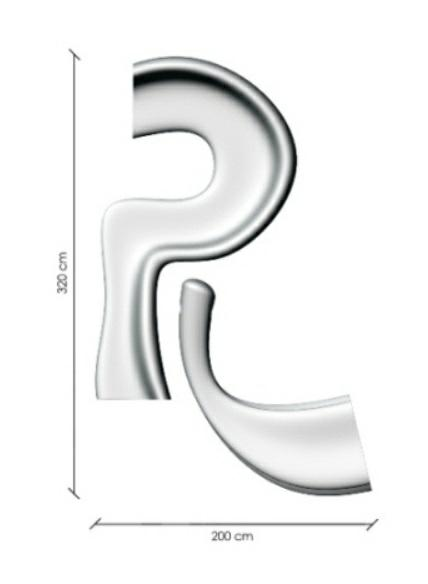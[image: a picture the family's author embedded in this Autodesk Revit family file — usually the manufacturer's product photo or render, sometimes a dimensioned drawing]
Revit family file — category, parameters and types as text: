
# Revit family: CITY ALPHABET litera „R”
name_source: partatom
category: Meble
revit_build: Autodesk Revit 2018 (Build: 20190510_1515(x64)
units: mm (PartAtom-declared; Revit-internal decimal feet)

## family parameters
Numer OmniClass = 23.40.10.11.14
Obiekt nadrzędny = Powierzchnia
Punkt obliczania pomieszczeń = Nie
Tnij formami wycięć po wczytaniu = Nie
Tytuł OmniClass = Exterior Seating
Współdzielony = Nie

## types (1)
- CITY ALPHABET litera „R”
    Domyślna rzędna = 1219 mm
    Długość = 2000 mm  [stored 6.56168 ft]
    IfcExportAs = IfcFurnishingElement
    Komentarze do typu = Ławka
    Materiał - informacja = Szeroki wybór kolorów wg palety RAL. Istnieje również możliwość specjalnego wykonania
kolorystycznego na indywidualne zapytanie klienta.
    Model = CITY ALPHABET litera „R”
    Obraz typu = R.jpg
    Producent = Astrini Design
    Szerokość = 3200 mm  [stored 10.4987 ft]
    Temepratura użytkowania = -40°C do 80°C, ( -40°F do 176°F )
    URL = http://astrini-design.pl
    Waga (szacunkowo) = 99.00 kg
    Waga po wypełnieniu (szacunkowo) = 199.00 kg
    Wysokość = 750 mm  [stored 2.46063 ft]

note: [stored X ft] marks values corroborated as IEEE doubles in the binary element streams (Revit-internal decimal feet)
